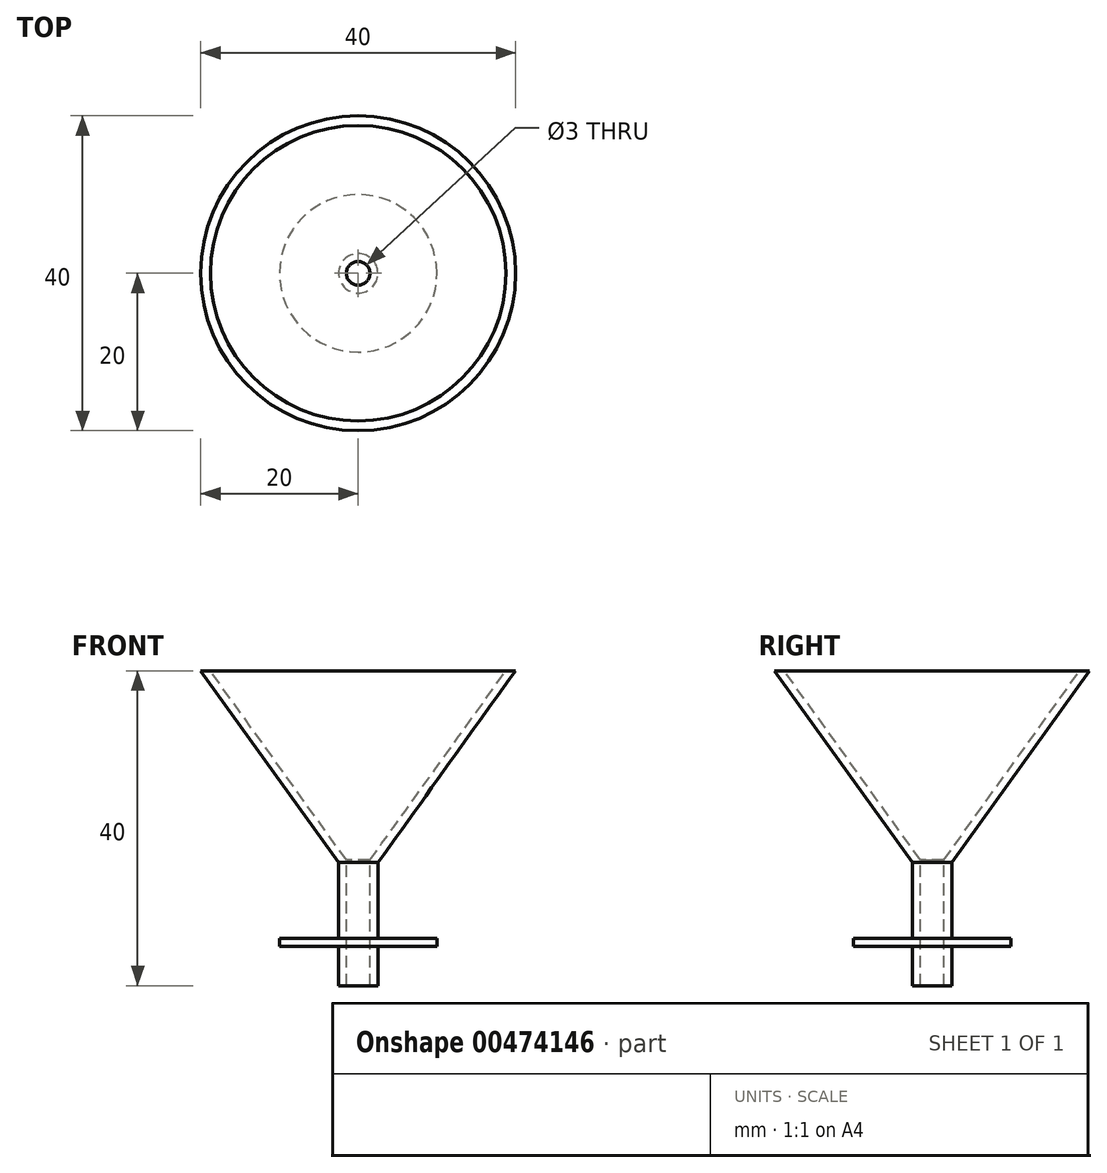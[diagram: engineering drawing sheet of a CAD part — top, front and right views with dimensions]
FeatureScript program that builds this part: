
annotation { "Feature Type Name" : "Feature", "Feature Type Description" : "" }
export const myFeature = defineFeature(function(context is Context, id is Id, definition is map)
    precondition{}
    {
        {
            var Q0;
            Q0=qCreatedBy(makeId("Front.planeOp"),FACE);
            var sketch = newSketch(context, id + "F0", { "sketchPlane" : qUnion([Q0])});
            skLineSegment(sketch, "E0.bottom", {"start": v(0, 40) * mm, "end": v(-2.5, 40) * mm});
            skLineSegment(sketch, "E0.top", {"start": v(0, 0) * mm, "end": v(-2.5, 0) * mm});
            skLineSegment(sketch, "E0.left", {"start": v(0, 40) * mm, "end": v(0, 0) * mm});
            skLineSegment(sketch, "E0.right", {"start": v(-2.5, 15.63) * mm, "end": v(-2.5, 6) * mm});
            skLineSegment(sketch, "E1.bottom", {"start": v(-2.5, 5) * mm, "end": v(-10, 5) * mm});
            skLineSegment(sketch, "E1.top", {"start": v(-2.5, 6) * mm, "end": v(-10, 6) * mm});
            skLineSegment(sketch, "E1.right", {"start": v(-10, 5) * mm, "end": v(-10, 6) * mm});
            skLineSegment(sketch, "E2.trimOffspring", {"start": v(-2.5, 5) * mm, "end": v(-2.5, 0) * mm});
            skLineSegment(sketch, "E3", {"start": v(-2.5, 40) * mm, "end": v(-20, 40) * mm});
            skLineSegment(sketch, "E4", {"start": v(-20, 40) * mm, "end": v(-2.5, 15.63) * mm});
            skLineSegment(sketch, "E5.0", {"start": v(-18.77, 40) * mm, "end": v(-1.5, 15.95) * mm});
            skLineSegment(sketch, "E6.0", {"start": v(-1.5, 15.95) * mm, "end": v(-1.5, 0) * mm});
            skSolve(sketch);
        }
        {
            var Q0;
            Q0=makeQuery(id+"F0.imprint","IMPRINT",FACE,{"disambiguationData":[TD([[makeQuery(id+"F0.imprint","IMPRINT",EDGE,{"derivedFrom":sQuery(id+"F0.wireOp",EDGE,"E0.right")}),1.0]])]});
            var Q1;
            Q1=sQuery(id+"F0.wireOp",EDGE,"E0.left");
            revolve(context, id + "F1", {"entities" : qUnion([Q0]), "axis" : qUnion([Q1]), "revolveType" : RevolveType.FULL});
        }
    });
